# Revit family: Кольцо с плитой низа
name_source: partatom
category: Обобщенные модели
revit_build: Autodesk Revit 2015 (Build: 20141119_1515(x64)
units: mm (PartAtom-declared; Revit-internal decimal feet)

## types (2) — shared parameters
Высота = 890 мм
Город и страна производства = Санкт-Петербург, Российская Федерация
Документ регламентирующий производство = ТУ 5855-001-23107031-2013
Изготовитель = ООО "ГИС"
Сайт изготовителя = http://gisspb.ru
Тип бетона = БСТ B20 П1 F200 W4 ГОСТ 7473-2010
Тип материалов покрытия = Полиэтилен низкого давления
Толщина футеровки = 4 мм

## per-type parameters (varying)
| type | Внешний диаметр | Внутрений диаметр | Внутрений диаметр по футеровке | Масса | Толщина основания | Толщина стенки |
| ДК-15.9 ФУТ "ПБК ЭКОВЭЛЛ" с анкерными листами V-Lock | 1680 мм | 1500 мм | 1492 мм | 1500.00 kg | 120 мм | 90 мм |
| ДК-10.9-ФУТ "ПБК ЭКОВЭЛЛ" с анкерными листами V-Lock | 1160 мм | 1000 мм | 992 мм | 850.00 kg | 100 мм | 80 мм |

## geometry (parser evidence)
native form markers: Blend x4
no freeform markers — native parametric forms only
